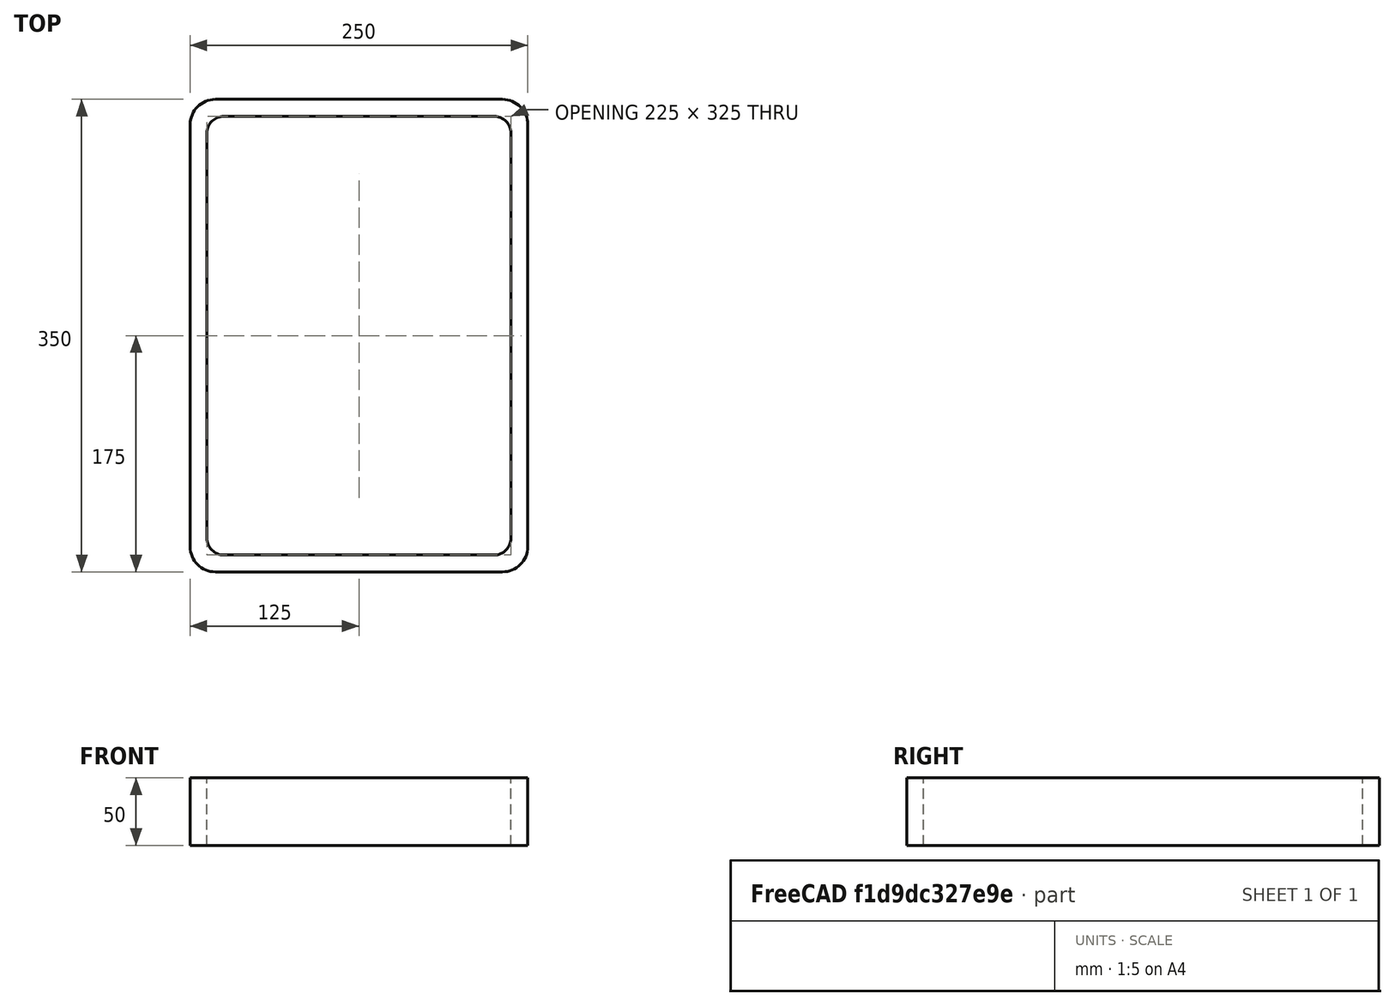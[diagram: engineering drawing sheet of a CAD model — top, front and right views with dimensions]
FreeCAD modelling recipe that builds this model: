
FCSTD DOCUMENT  (FreeCAD 0.15R4671 (Git))
Label: Rectangular hollow section 350x250x12.5 EN10219 S235JRH
License: All rights reserved
LicenseURL: http://en.wikipedia.org/wiki/All_rights_reserved
objects: Sketcher::SketchObject×1, Part::Extrusion×1
note: 2 computed .brp shape members not serialized (recipe doc carries the construction recipe); baked Part::Feature solids carry a one-line shape summary decoded from their .brp

FEATURE [Sketcher::SketchObject] Sketch
  sketch-geometry (16):
    g0: LineSegment StartX=-100 StartY=162.5 StartZ=0 EndX=100 EndY=162.5 EndZ=0
    g1: LineSegment StartX=112.5 StartY=150 StartZ=0 EndX=112.5 EndY=-150 EndZ=0
    g2: LineSegment StartX=100 StartY=-162.5 StartZ=0 EndX=-100 EndY=-162.5 EndZ=0
    g3: LineSegment StartX=-112.5 StartY=-150 StartZ=0 EndX=-112.5 EndY=150 EndZ=0
    g4: LineSegment StartX=-106.25 StartY=175 StartZ=0 EndX=106.25 EndY=175 EndZ=0
    g5: LineSegment StartX=125 StartY=156.25 StartZ=0 EndX=125 EndY=-156.25 EndZ=0
    g6: LineSegment StartX=106.25 StartY=-175 StartZ=0 EndX=-106.25 EndY=-175 EndZ=0
    g7: LineSegment StartX=-125 StartY=-156.25 StartZ=0 EndX=-125 EndY=156.25 EndZ=0
    g8: ArcOfCircle CenterX=-100 CenterY=150 CenterZ=0 NormalX=0 NormalY=0 NormalZ=1 Radius=12.5 StartAngle=1.5708 EndAngle=3.14159
    g9: ArcOfCircle CenterX=100 CenterY=150 CenterZ=0 NormalX=0 NormalY=0 NormalZ=1 Radius=12.5 StartAngle=0 EndAngle=1.5708
    g10: ArcOfCircle CenterX=100 CenterY=-150 CenterZ=0 NormalX=0 NormalY=0 NormalZ=1 Radius=12.5 StartAngle=4.71239 EndAngle=6.28319
    g11: ArcOfCircle CenterX=-100 CenterY=-150 CenterZ=0 NormalX=0 NormalY=0 NormalZ=1 Radius=12.5 StartAngle=3.14159 EndAngle=4.71239
    g12: ArcOfCircle CenterX=106.25 CenterY=156.25 CenterZ=0 NormalX=0 NormalY=0 NormalZ=1 Radius=18.75 StartAngle=0 EndAngle=1.5708
    g13: ArcOfCircle CenterX=106.25 CenterY=-156.25 CenterZ=0 NormalX=0 NormalY=0 NormalZ=1 Radius=18.75 StartAngle=4.71239 EndAngle=6.28319
    g14: ArcOfCircle CenterX=-106.25 CenterY=-156.25 CenterZ=0 NormalX=0 NormalY=0 NormalZ=1 Radius=18.75 StartAngle=3.14159 EndAngle=4.71239
    g15: ArcOfCircle CenterX=-106.25 CenterY=156.25 CenterZ=0 NormalX=0 NormalY=0 NormalZ=1 Radius=18.75 StartAngle=1.5708 EndAngle=3.14159
  constraints (36):
    c: Horizontal(g2)
    c: Vertical(g3)
    c: Horizontal(g6)
    c: Vertical(g7)
    c: Tangent(g3,g8) = 1.5708
    c: Tangent(g0,g8) = 1.5708
    c: Tangent(g0,g9) = 1.5708
    c: Tangent(g1,g9) = 1.5708
    c: Tangent(g1,g10) = 1.5708
    c: Tangent(g2,g10) = 1.5708
    c: Tangent(g2,g11) = 1.5708
    c: Tangent(g3,g11) = 1.5708
    c: Tangent(g4,g12) = 1.5708
    c: Tangent(g5,g12) = 1.5708
    c: Tangent(g5,g13) = 1.5708
    c: Tangent(g6,g13) = 1.5708
    c: Tangent(g6,g14) = 1.5708
    c: Tangent(g7,g14) = 1.5708
    c: Tangent(g7,g15) = 1.5708
    c: Tangent(g4,g15) = 1.5708
    c: Equal(g9,g8)
    c: Equal(g9,g11)
    c: Equal(g9,g10)
    c: Equal(g12,g15)
    c: Equal(g12,g14)
    c: Equal(g12,g13)
    c: Symmetric(g4,g6,g-1)
    c: Symmetric(g7,g5,g-2)
    c: DistanceY(g4,g6) = -350
    c: DistanceX(g7,g5) = 250
    c: Symmetric(g3,g1,g-2)
    c: Symmetric(g0,g2,g-1)
    c: DistanceY(g0,g4) = 12.5
    c: DistanceX(g5,g1) = -12.5
    c: Radius(g9) = 12.5
    c: Radius(g12) = 18.75
FEATURE [Part::Extrusion] Extrude  label="Rectangular hollow section 350x250x12.5 EN10219 S235JRH"
  Base = -> Sketch
  Dir = (0,0,50)
  Solid = true
